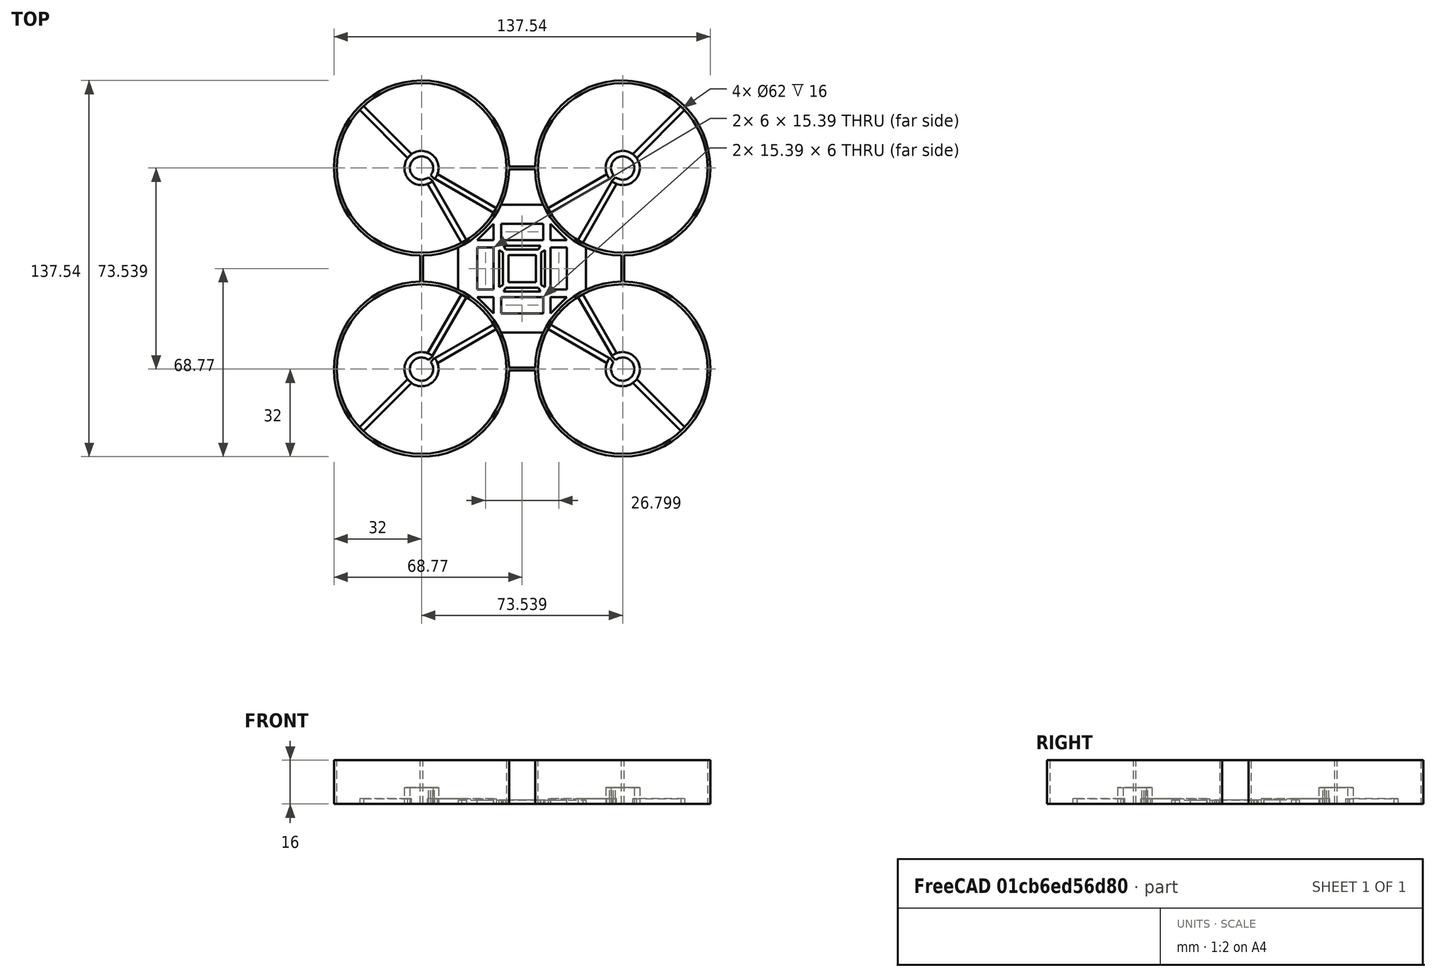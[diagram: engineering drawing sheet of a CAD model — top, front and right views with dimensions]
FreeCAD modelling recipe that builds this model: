
FCSTD DOCUMENT  (FreeCAD 0.19R23578 (Git))
Label: body
License: All rights reserved
LicenseURL: http://en.wikipedia.org/wiki/All_rights_reserved
objects: Part::Feature×28, Part::Extrusion×28, Part::Cut×18, Part::MultiFuse×1
note: 75 computed .brp shape members not serialized (recipe doc carries the construction recipe); baked Part::Feature solids carry a one-line shape summary decoded from their .brp

FEATURE [Part::Feature] Face011
  shape: bbox 6 x 6 x 2e-07 mm, 1 faces, 0 solids (baked)
FEATURE [Part::Feature] Face010
  shape: bbox 6 x 15.39 x 2e-07 mm, 1 faces, 0 solids (baked)
FEATURE [Part::Feature] Face005
  shape: bbox 1.4 x 13.4 x 2e-07 mm, 1 faces, 0 solids (baked)
FEATURE [Part::Feature] Face008
  shape: bbox 13.4 x 1.4 x 2e-07 mm, 1 faces, 0 solids (baked)
FEATURE [Part::Feature] Face013
  shape: bbox 46.8 x 46.8 x 2e-07 mm, 1 faces, 0 solids (baked)
FEATURE [Part::Feature] Face012
  shape: bbox 15.39 x 6 x 2e-07 mm, 1 faces, 0 solids (baked)
FEATURE [Part::Extrusion] Extrude
  Base = -> Face013
  Dir = (0,0,1)
  DirMode = 0
  FaceMakerClass = Part::FaceMakerBullseye
  LengthFwd = 1.5
  LengthRev = 0
  Solid = false
  Symmetric = false
FEATURE [Part::Extrusion] Extrude006
  Base = -> Face005
  Dir = (0,0,1)
  DirMode = 0
  FaceMakerClass = Part::FaceMakerBullseye
  LengthFwd = 3
  LengthRev = 0
  Solid = false
  Symmetric = false
FEATURE [Part::Extrusion] Extrude009
  Base = -> Face008
  Dir = (0,0,1)
  DirMode = 0
  FaceMakerClass = Part::FaceMakerBullseye
  LengthFwd = 3
  LengthRev = 0
  Solid = false
  Symmetric = false
FEATURE [Part::Extrusion] Extrude011
  Base = -> Face010
  Dir = (0,0,1)
  DirMode = 0
  FaceMakerClass = Part::FaceMakerBullseye
  LengthFwd = 3
  LengthRev = 0
  Solid = false
  Symmetric = false
FEATURE [Part::Extrusion] Extrude012
  Base = -> Face011
  Dir = (0,0,1)
  DirMode = 0
  FaceMakerClass = Part::FaceMakerBullseye
  LengthFwd = 3
  LengthRev = 0
  Solid = false
  Symmetric = false
FEATURE [Part::Extrusion] Extrude013
  Base = -> Face012
  Dir = (0,0,1)
  DirMode = 0
  FaceMakerClass = Part::FaceMakerBullseye
  LengthFwd = 3
  LengthRev = 0
  Solid = false
  Symmetric = false
FEATURE [Part::Cut] Cut
  Base = -> Extrude
  Tool = -> Extrude011
FEATURE [Part::Cut] Cut001
  Base = -> Cut
  Tool = -> Extrude013
FEATURE [Part::Feature] Face006
  shape: bbox 13.4 x 1.4 x 2e-07 mm, 1 faces, 0 solids (baked)
FEATURE [Part::Extrusion] Extrude007
  Base = -> Face006
  Dir = (0,0,1)
  DirMode = 0
  FaceMakerClass = Part::FaceMakerBullseye
  LengthFwd = 3
  LengthRev = 0
  Solid = false
  Symmetric = false
FEATURE [Part::Cut] Cut002
  Base = -> Cut001
  Tool = -> Extrude012
FEATURE [Part::Feature] Face007
  shape: bbox 10 x 10 x 2e-07 mm, 1 faces, 0 solids (baked)
FEATURE [Part::Extrusion] Extrude008
  Base = -> Face007
  Dir = (0,0,1)
  DirMode = 0
  FaceMakerClass = Part::FaceMakerBullseye
  LengthFwd = 3
  LengthRev = 0
  Solid = false
  Symmetric = false
FEATURE [Part::Feature] Face002
  shape: bbox 6 x 6 x 2e-07 mm, 1 faces, 0 solids (baked)
FEATURE [Part::Extrusion] Extrude003
  Base = -> Face002
  Dir = (0,0,1)
  DirMode = 0
  FaceMakerClass = Part::FaceMakerBullseye
  LengthFwd = 3
  LengthRev = 0
  Solid = false
  Symmetric = false
FEATURE [Part::Feature] Face001
  shape: bbox 15.39 x 6 x 2e-07 mm, 1 faces, 0 solids (baked)
FEATURE [Part::Extrusion] Extrude002
  Base = -> Face001
  Dir = (0,0,1)
  DirMode = 0
  FaceMakerClass = Part::FaceMakerBullseye
  LengthFwd = 3
  LengthRev = 0
  Solid = false
  Symmetric = false
FEATURE [Part::Feature] Face004
  shape: bbox 6 x 6 x 2e-07 mm, 1 faces, 0 solids (baked)
FEATURE [Part::Extrusion] Extrude005
  Base = -> Face004
  Dir = (0,0,1)
  DirMode = 0
  FaceMakerClass = Part::FaceMakerBullseye
  LengthFwd = 3
  LengthRev = 0
  Solid = false
  Symmetric = false
FEATURE [Part::Feature] Face
  shape: bbox 6 x 6 x 2e-07 mm, 1 faces, 0 solids (baked)
FEATURE [Part::Extrusion] Extrude001
  Base = -> Face
  Dir = (0,0,1)
  DirMode = 0
  FaceMakerClass = Part::FaceMakerBullseye
  LengthFwd = 3
  LengthRev = 0
  Solid = false
  Symmetric = false
FEATURE [Part::Feature] Face009
  shape: bbox 1.4 x 13.4 x 2e-07 mm, 1 faces, 0 solids (baked)
FEATURE [Part::Extrusion] Extrude010
  Base = -> Face009
  Dir = (0,0,1)
  DirMode = 0
  FaceMakerClass = Part::FaceMakerBullseye
  LengthFwd = 3
  LengthRev = 0
  Solid = false
  Symmetric = false
FEATURE [Part::Cut] Cut003
  Base = -> Cut002
  Tool = -> Extrude010
FEATURE [Part::Cut] Cut004
  Base = -> Cut003
  Tool = -> Extrude009
FEATURE [Part::Cut] Cut005
  Base = -> Cut004
  Tool = -> Extrude008
FEATURE [Part::Cut] Cut006
  Base = -> Cut005
  Tool = -> Extrude007
FEATURE [Part::Cut] Cut007
  Base = -> Cut006
  Tool = -> Extrude006
FEATURE [Part::Cut] Cut008
  Base = -> Cut007
  Tool = -> Extrude005
FEATURE [Part::Feature] Face003
  shape: bbox 6 x 15.39 x 2e-07 mm, 1 faces, 0 solids (baked)
FEATURE [Part::Extrusion] Extrude004
  Base = -> Face003
  Dir = (0,0,1)
  DirMode = 0
  FaceMakerClass = Part::FaceMakerBullseye
  LengthFwd = 3
  LengthRev = 0
  Solid = false
  Symmetric = false
FEATURE [Part::Cut] Cut009
  Base = -> Cut008
  Tool = -> Extrude004
FEATURE [Part::Cut] Cut010
  Base = -> Cut009
  Tool = -> Extrude003
FEATURE [Part::Cut] Cut011
  Base = -> Cut010
  Tool = -> Extrude002
FEATURE [Part::Cut] Cut012
  Base = -> Cut011
  Tool = -> Extrude001
FEATURE [Part::Feature] Face014
  shape: bbox 50.74 x 50.74 x 2e-07 mm, 1 faces, 0 solids (baked)
FEATURE [Part::Feature] Face015
  shape: bbox 50.74 x 50.74 x 2e-07 mm, 1 faces, 0 solids (baked)
FEATURE [Part::Feature] Face016
  shape: bbox 50.74 x 50.74 x 2e-07 mm, 1 faces, 0 solids (baked)
FEATURE [Part::Extrusion] Extrude014
  Base = -> Face016
  Dir = (0,0,1)
  DirMode = 0
  FaceMakerClass = Part::FaceMakerBullseye
  LengthFwd = 2
  LengthRev = 0
  Solid = false
  Symmetric = false
FEATURE [Part::Extrusion] Extrude015
  Base = -> Face014
  Dir = (0,0,1)
  DirMode = 0
  FaceMakerClass = Part::FaceMakerBullseye
  LengthFwd = 2
  LengthRev = 0
  Solid = false
  Symmetric = false
FEATURE [Part::Extrusion] Extrude016
  Base = -> Face015
  Dir = (0,0,1)
  DirMode = 0
  FaceMakerClass = Part::FaceMakerBullseye
  LengthFwd = 2
  LengthRev = 0
  Solid = false
  Symmetric = false
FEATURE [Part::Feature] Face017
  shape: bbox 50.74 x 50.74 x 2e-07 mm, 1 faces, 0 solids (baked)
FEATURE [Part::Extrusion] Extrude017
  Base = -> Face017
  Dir = (0,0,1)
  DirMode = 0
  FaceMakerClass = Part::FaceMakerBullseye
  LengthFwd = 2
  LengthRev = 0
  Solid = false
  Symmetric = false
FEATURE [Part::Feature] Face018
  shape: bbox 12.5 x 12.5 x 2e-07 mm, 1 faces, 0 solids (baked)
FEATURE [Part::Feature] Face019
  shape: bbox 12.5 x 12.5 x 2e-07 mm, 1 faces, 0 solids (baked)
FEATURE [Part::Feature] Face020
  shape: bbox 12.5 x 12.5 x 2e-07 mm, 1 faces, 0 solids (baked)
FEATURE [Part::Extrusion] Extrude019
  Base = -> Face019
  Dir = (0,0,1)
  DirMode = 0
  FaceMakerClass = Part::FaceMakerBullseye
  LengthFwd = 6
  LengthRev = 0
  Solid = false
  Symmetric = false
FEATURE [Part::Extrusion] Extrude020
  Base = -> Face020
  Dir = (0,0,1)
  DirMode = 0
  FaceMakerClass = Part::FaceMakerBullseye
  LengthFwd = 6
  LengthRev = 0
  Solid = false
  Symmetric = false
FEATURE [Part::Extrusion] Extrude021
  Base = -> Face018
  Dir = (0,0,1)
  DirMode = 0
  FaceMakerClass = Part::FaceMakerBullseye
  LengthFwd = 6
  LengthRev = 0
  Solid = false
  Symmetric = false
FEATURE [Part::Feature] Face021
  shape: bbox 12.5 x 12.5 x 2e-07 mm, 1 faces, 0 solids (baked)
FEATURE [Part::Extrusion] Extrude018
  Base = -> Face021
  Dir = (0,0,1)
  DirMode = 0
  FaceMakerClass = Part::FaceMakerBullseye
  LengthFwd = 6
  LengthRev = 0
  Solid = false
  Symmetric = false
FEATURE [Part::Feature] Face022
  shape: bbox 72.54 x 72.54 x 2e-07 mm, 1 faces, 0 solids (baked)
FEATURE [Part::Feature] Shape002
  shape: bbox 62 x 62 x 2e-07 mm, 0 faces, 0 solids (baked)
FEATURE [Part::Feature] Shape003
  shape: bbox 62 x 62 x 2e-07 mm, 0 faces, 0 solids (baked)
FEATURE [Part::Feature] Shape
  shape: bbox 62 x 62 x 2e-07 mm, 0 faces, 0 solids (baked)
FEATURE [Part::Feature] Shape001
  shape: bbox 62 x 62 x 2e-07 mm, 0 faces, 0 solids (baked)
FEATURE [Part::Extrusion] Extrude023
  Base = -> Shape
  Dir = (0,0,1)
  DirMode = 0
  FaceMakerClass = Part::FaceMakerBullseye
  LengthFwd = 20
  LengthRev = 0
  Solid = true
  Symmetric = false
FEATURE [Part::Extrusion] Extrude024
  Base = -> Shape001
  Dir = (0,0,1)
  DirMode = 0
  FaceMakerClass = Part::FaceMakerBullseye
  LengthFwd = 20
  LengthRev = 0
  Solid = true
  Symmetric = false
FEATURE [Part::Extrusion] Extrude025
  Base = -> Shape002
  Dir = (0,0,1)
  DirMode = 0
  FaceMakerClass = Part::FaceMakerBullseye
  LengthFwd = 20
  LengthRev = 0
  Solid = true
  Symmetric = false
FEATURE [Part::Extrusion] Extrude026
  Base = -> Shape003
  Dir = (0,0,1)
  DirMode = 0
  FaceMakerClass = Part::FaceMakerBullseye
  LengthFwd = 20
  LengthRev = 0
  Solid = true
  Symmetric = false
FEATURE [Part::Extrusion] Extrude027
  Base = -> Face022
  Dir = (0,0,1)
  DirMode = 0
  FaceMakerClass = Part::FaceMakerBullseye
  LengthFwd = 20
  LengthRev = 0
  Solid = true
  Symmetric = false
FEATURE [Part::Feature] Face023
  shape: bbox 137.5 x 137.5 x 2e-07 mm, 1 faces, 0 solids (baked)
FEATURE [Part::Extrusion] Extrude022
  Base = -> Face023
  Dir = (0,0,1)
  DirMode = 0
  FaceMakerClass = Part::FaceMakerBullseye
  LengthFwd = 16
  LengthRev = 0
  Solid = false
  Symmetric = false
FEATURE [Part::Cut] Cut013
  Base = -> Extrude022
  Tool = -> Extrude023
FEATURE [Part::Cut] Cut015
  Base = -> Cut013
  Tool = -> Extrude027
FEATURE [Part::Cut] Cut017
  Base = -> Cut015
  Tool = -> Extrude026
FEATURE [Part::Cut] Cut016
  Base = -> Cut017
  Tool = -> Extrude025
FEATURE [Part::Cut] Cut014
  Base = -> Cut016
  Tool = -> Extrude024
FEATURE [Part::MultiFuse] Fusion
  Shapes = -> [Cut012,Extrude014,Extrude015,Extrude016,Extrude017,Extrude018,Extrude019,Extrude020,Extrude021,Cut014]
